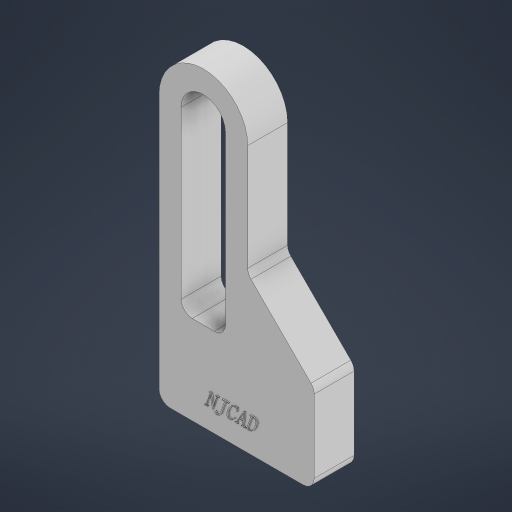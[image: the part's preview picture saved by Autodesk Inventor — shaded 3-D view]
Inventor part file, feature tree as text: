
AUTODESK INVENTOR PART (.ipt)
format: ipt  version: 2023 (Build 270158000, 158)  size: 351,232 bytes
history: native  units: mm
features: sketch x2, extrude x1, fillet x1, emboss x1
ambient origin geometry x8: Origin, YZ Plane, XZ Plane, XY Plane, X Axis, Y Axis, Z Axis, Center Point
bodies: Solid1 (feature_tree)
feature tree (5):
  extrude  "Extrusion1"  Depth=120.0mm
  fillet  "Fillet1"  Radius=30.0mm
  emboss  "Emboss1"
  sketch  "Sketch1"  dims[d2=30.0mm d8=120.0mm d11=30.0mm]
  sketch  "Sketch2"  dims[d13=30.0mm d15=30.0mm d16=40.0mm d17=20.0mm d20=40.0mm d21=70.0mm d22=80.0mm d23=20.0mm d24=18.0mm d25=0.0mm d26=5.0mm d27=0.5mm d28=0.0mm]
